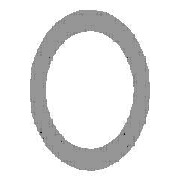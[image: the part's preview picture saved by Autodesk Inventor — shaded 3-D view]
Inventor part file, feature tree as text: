
AUTODESK INVENTOR PART (.ipt)
format: ipt  version: 2013 (Build 170138000, 138)  size: 107,520 bytes
history: native  units: mm (DEFAULTED — no unit token found)
features: other x4, sketch x3, plane x1
ambient origin geometry x8: Origin, YZ Plane, XZ Plane, XY Plane, X Axis, Y Axis, Z Axis, Center Point
bodies: Solid1 (feature_tree), Body (feature_tree)
feature tree (8):
  parser-record x1  (decoder bookkeeping rows leaked as tree rows — omitted from the tree; the rows remain in map.json)
  other  "Driven Length"
  other  "Start plane"
  other  "End plane"
  sketch  "Sketch"  dims[d2=2143.252mm d3=0.0mm d4=-0.0mm d5=2143.252mm d6=90.0deg d7=2143.252mm]
  sketch  "Sketch3"  dims[d0=33.401mm]
  plane  "Work Plane3"
  sketch  "Sketch4"  dims[d1=3.3782mm]
